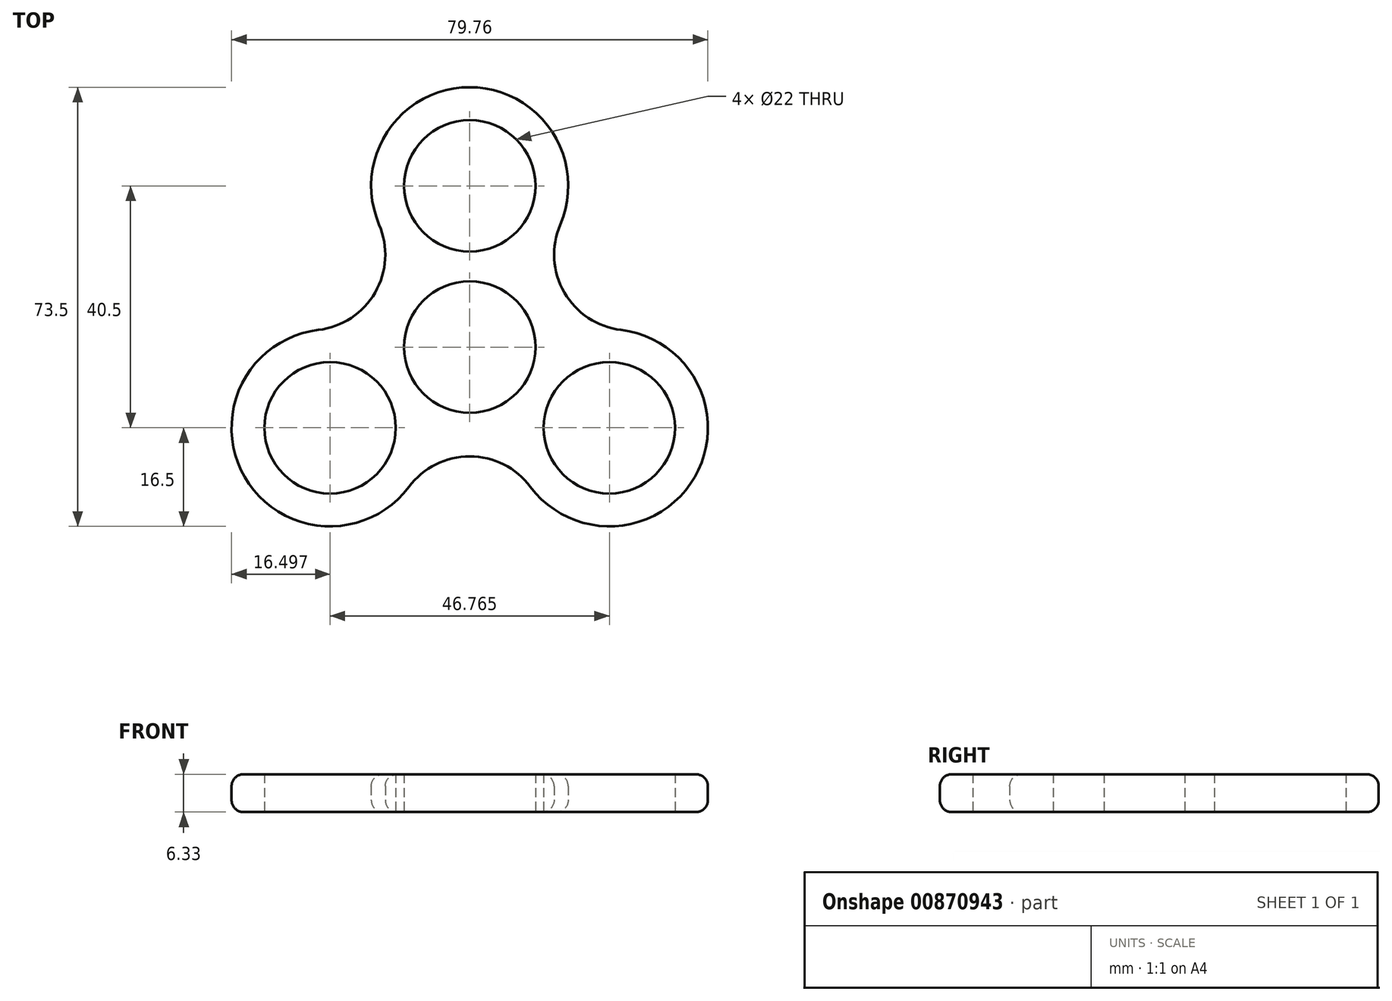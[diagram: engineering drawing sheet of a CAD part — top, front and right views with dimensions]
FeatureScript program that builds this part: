
annotation { "Feature Type Name" : "Feature", "Feature Type Description" : "" }
export const myFeature = defineFeature(function(context is Context, id is Id, definition is map)
    precondition{}
    {
        {
            var Q0;
            Q0=qCreatedBy(makeId("Top.planeOp"),FACE);
            var sketch = newSketch(context, id + "F0", { "sketchPlane" : qUnion([Q0])});
            skLineSegment(sketch, "E0", {"start": v(0, 0) * mm, "end": v(0, 27) * mm, "construction": true});
            skLineSegment(sketch, "E1", {"start": v(0, 0) * mm, "end": v(23.38, -13.5) * mm, "construction": true});
            skLineSegment(sketch, "E2", {"start": v(0, 0) * mm, "end": v(-23.38, -13.5) * mm, "construction": true});
            skCircle(sketch, "E3", {"center": v(0, 0) * mm, "radius": 27 * mm, "construction": true});
            skCircle(sketch, "E4", {"center": v(23.38, -13.5) * mm, "radius": 11 * mm});
            skCircle(sketch, "E5", {"center": v(-23.38, -13.5) * mm, "radius": 11 * mm});
            skCircle(sketch, "E6", {"center": v(0, 27) * mm, "radius": 11 * mm});
            skCircle(sketch, "E7", {"center": v(0, 0) * mm, "radius": 11 * mm});
            skCircle(sketch, "E8", {"center": v(0, 27) * mm, "radius": 16.5 * mm});
            skCircle(sketch, "E9", {"center": v(-23.38, -13.5) * mm, "radius": 16.5 * mm});
            skCircle(sketch, "E10", {"center": v(23.38, -13.5) * mm, "radius": 16.5 * mm});
            skCircle(sketch, "E11", {"center": v(-26.84, 15.5) * mm, "radius": 12.7 * mm});
            skCircle(sketch, "E12", {"center": v(0, -30.99) * mm, "radius": 12.7 * mm});
            skCircle(sketch, "E13", {"center": v(26.84, 15.5) * mm, "radius": 12.7 * mm});
            skSolve(sketch);
        }
        {
            var Q0;
            Q0=qCreatedBy(makeId("Top.planeOp"),FACE);
            var sketch = newSketch(context, id + "F1", { "sketchPlane" : qUnion([Q0])});
            skArc(sketch, "E14.0", {"start": v(15.17, 20.5) * mm, "mid": v(0, 43.5) * mm, "end": v(-15.17, 20.5) * mm});
            skArc(sketch, "E14.1", {"start": v(-25.34, 2.88) * mm, "mid": v(-15.84, 9.14) * mm, "end": v(-15.17, 20.5) * mm});
            skArc(sketch, "E14.2", {"start": v(-25.34, 2.88) * mm, "mid": v(-37.67, -21.75) * mm, "end": v(-10.17, -23.38) * mm});
            skArc(sketch, "E14.3", {"start": v(10.17, -23.38) * mm, "mid": v(0, -18.29) * mm, "end": v(-10.17, -23.38) * mm});
            skArc(sketch, "E14.4", {"start": v(10.17, -23.38) * mm, "mid": v(37.67, -21.75) * mm, "end": v(25.34, 2.88) * mm});
            skArc(sketch, "E14.5", {"start": v(15.17, 20.5) * mm, "mid": v(15.84, 9.14) * mm, "end": v(25.34, 2.88) * mm});
            skSolve(sketch);
        }
        {
            var Q0;
            Q0 = qSketchRegion(id + "F1", true);
            extrude(context, id + "F2", {"entities" : qUnion([Q0]), "depth" : 6.33 * mm, "offsetDistance" : 25 * mm});
        }
        {
            var Q0;
            Q0=qCreatedBy(makeId("Top.planeOp"),FACE);
            var sketch = newSketch(context, id + "F3", { "sketchPlane" : qUnion([Q0])});
            skCircle(sketch, "E15.0", {"center": v(-23.38, -13.5) * mm, "radius": 11 * mm});
            skCircle(sketch, "E15.1", {"center": v(0, 27) * mm, "radius": 11 * mm});
            skCircle(sketch, "E15.2", {"center": v(23.38, -13.5) * mm, "radius": 11 * mm});
            skCircle(sketch, "E15.3", {"center": v(0, 0) * mm, "radius": 11 * mm});
            skSolve(sketch);
        }
        {
            var Q0;
            Q0 = qSketchRegion(id + "F3", true);
            extrude(context, id + "F4", {"entities" : qUnion([Q0]), "operationType" : NewBodyOperationType.REMOVE, "endBound" : BoundingType.THROUGH_ALL, "depth" : 25 * mm, "offsetDistance" : 25 * mm});
        }
        {
            var Q0;
            Q0=makeQuery(id+"F2.opExtrude","CAP_EDGE",EDGE,{"disambiguationData":[OSD([sQuery(id+"F1.wireOp",EDGE,"E14.0")])],"isStart":false});
            var Q1;
            Q1=makeQuery(id+"F2.opExtrude","CAP_EDGE",EDGE,{"disambiguationData":[OSD([sQuery(id+"F1.wireOp",EDGE,"E14.1")])],"isStart":false});
            var Q2;
            Q2=makeQuery(id+"F2.opExtrude","CAP_EDGE",EDGE,{"disambiguationData":[OSD([sQuery(id+"F1.wireOp",EDGE,"E14.2")])],"isStart":true});
            fillet(context, id + "F5", {"entities" : qUnion([Q0, Q1, Q2]), "radius" : 2 * mm, "tangentPropagation" : true, "allowEdgeOverflow" : false});
        }
    });
